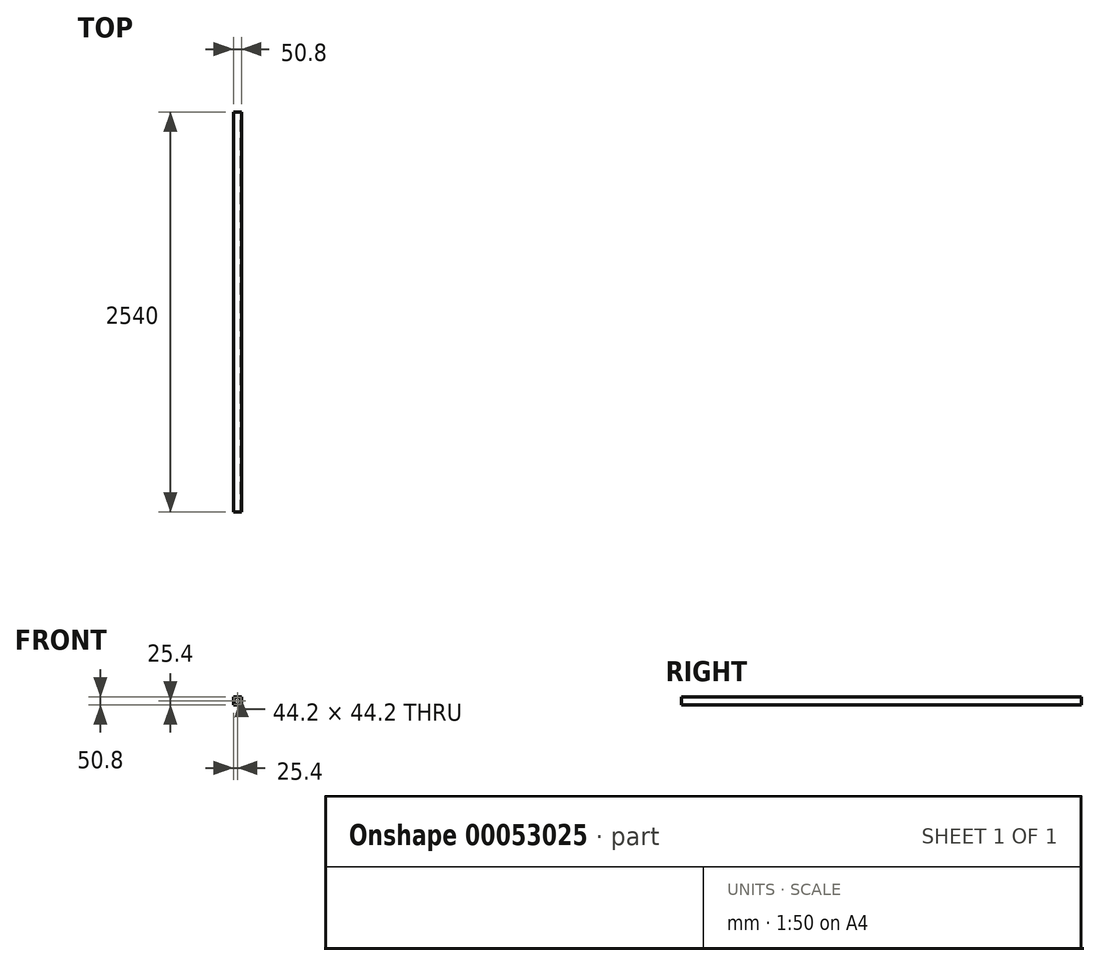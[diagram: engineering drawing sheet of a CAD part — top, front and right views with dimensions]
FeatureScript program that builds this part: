
annotation { "Feature Type Name" : "Feature", "Feature Type Description" : "" }
export const myFeature = defineFeature(function(context is Context, id is Id, definition is map)
    precondition{}
    {
        {
            var Q0;
            Q0=qCreatedBy(makeId("Front.planeOp"),FACE);
            var sketch = newSketch(context, id + "F0", { "sketchPlane" : qUnion([Q0])});
            skLineSegment(sketch, "E0.bottom", {"start": v(0, 0) * mm, "end": v(-50.8, 0) * mm});
            skLineSegment(sketch, "E0.top", {"start": v(0, 50.8) * mm, "end": v(-50.8, 50.8) * mm});
            skLineSegment(sketch, "E0.left", {"start": v(0, 0) * mm, "end": v(0, 50.8) * mm});
            skLineSegment(sketch, "E0.right", {"start": v(-50.8, 0) * mm, "end": v(-50.8, 50.8) * mm});
            skLineSegment(sketch, "E1.bottom", {"start": v(-3.3, 3.3) * mm, "end": v(-47.5, 3.3) * mm});
            skLineSegment(sketch, "E1.top", {"start": v(-3.3, 47.5) * mm, "end": v(-47.5, 47.5) * mm});
            skLineSegment(sketch, "E1.left", {"start": v(-3.3, 3.3) * mm, "end": v(-3.3, 47.5) * mm});
            skLineSegment(sketch, "E1.right", {"start": v(-47.5, 3.3) * mm, "end": v(-47.5, 47.5) * mm});
            skSolve(sketch);
        }
        {
            var Q0;
            Q0=makeQuery(id+"F0.imprint","IMPRINT",FACE,{"disambiguationData":[TD([[makeQuery(id+"F0.imprint","IMPRINT",EDGE,{"derivedFrom":sQuery(id+"F0.wireOp",EDGE,"E0.bottom")}),-1.0]])]});
            extrude(context, id + "F1", {"entities" : qUnion([Q0]), "depth" : 2540 * mm});
        }
    });
